# Revit family: Toilet_Seat-Elongated_Closed_Front-Cleansing-KOHLER-C3-035-K-28010K_1
name_source: partatom
category: Plumbing Fixtures
revit_build: Autodesk Revit 2017 (Build: 20160225_1515(x64)
units: mm (PartAtom-declared; Revit-internal decimal feet)

## family parameters
Cut with Voids When Loaded = No
Host = Face
OmniClass Number = 23.31.19.19.19
OmniClass Title = Water Closet Tanks
Part Type = Normal
Room Calculation Point = No
Round Connector Dimension = Use Diameter
Shared = No

## types (1)
- 0-White
    ADA Compliant = No
    Assembly Code = D2010100
    CW Connection = Yes
    Cold Water Inlet = Cold Water Inlet
    Date Modified = 12/31/2021
    Default Elevation = 15"
    Description = MANUAL BIDET SEAT
    Finish = Kohler-Plastic-0-White
    Flow Rate = 0 GPM
    HW Connection = No
    Height = 3 1/16"
    Hot Water Inlet = Hot Water Inlet
    Length = 19 15/16"
    Manufacturer = KOHLER Co.
    Master Format 2014 = 22 42 13.13
    Master Format 2014 Name = Toilet, Bath, and Laundry Accessories
    Material = Plastic
    Model = K-28010K-0
    Pressure = 0.00 psi
    Product Name = C3-035
    Type = 1
    URL = https://www.kohlerasiapacific.com
    Vent Connection = No
    Waste Connection = No
    WaterSense Certified = No
    Width = 14 1/2"

## geometry (parser evidence)
native form markers: Sweep x4
no freeform markers — native parametric forms only
